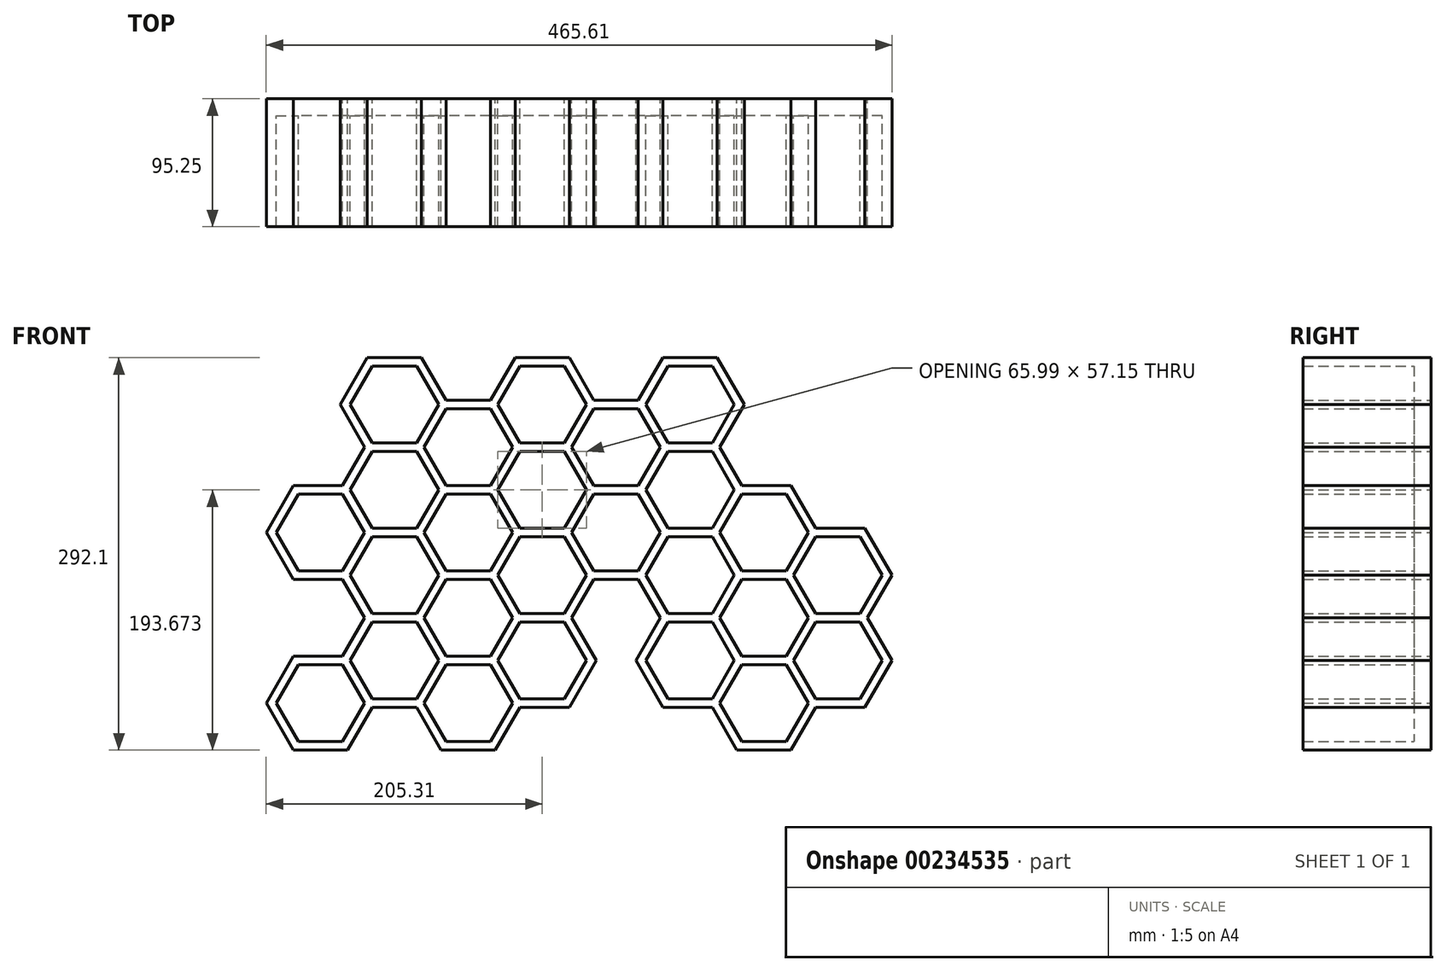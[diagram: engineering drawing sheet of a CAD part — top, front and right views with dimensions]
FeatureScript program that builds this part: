
annotation { "Feature Type Name" : "Feature", "Feature Type Description" : "" }
export const myFeature = defineFeature(function(context is Context, id is Id, definition is map)
    precondition{}
    {
        {
            var Q0;
            Q0=qCreatedBy(makeId("Front.planeOp"),FACE);
            var sketch = newSketch(context, id + "F0", { "sketchPlane" : qUnion([Q0])});
            skLineSegment(sketch, "E0.1", {"start": v(-4.28, 35.04) * mm, "end": v(27.5, 35.04) * mm});
            skCircle(sketch, "E1.cCircle", {"center": v(-40.94, 35.04) * mm, "radius": 28.58 * mm, "construction": true});
            skLineSegment(sketch, "E1.0", {"start": v(-73.94, 35.04) * mm, "end": v(-57.44, 63.62) * mm});
            skLineSegment(sketch, "E1.1", {"start": v(-57.44, 63.62) * mm, "end": v(-24.44, 63.62) * mm});
            skLineSegment(sketch, "E1.2", {"start": v(-24.44, 63.62) * mm, "end": v(-7.94, 35.04) * mm});
            skLineSegment(sketch, "E1.3", {"start": v(-7.94, 35.04) * mm, "end": v(-24.44, 6.47) * mm});
            skLineSegment(sketch, "E1.4", {"start": v(-24.44, 6.47) * mm, "end": v(-57.44, 6.47) * mm});
            skLineSegment(sketch, "E1.5", {"start": v(-57.44, 6.47) * mm, "end": v(-73.94, 35.04) * mm});
            skPoint(sketch, "E1.0.midPoint", {"position": v(-65.69, 49.33) * mm});
            skCircle(sketch, "E2.cCircle", {"center": v(-40.94, 35.04) * mm, "radius": 31.75 * mm, "construction": true});
            skLineSegment(sketch, "E2.0", {"start": v(-77.6, 35.04) * mm, "end": v(-59.27, 66.8) * mm});
            skLineSegment(sketch, "E2.1", {"start": v(-59.27, 66.8) * mm, "end": v(-22.6, 66.8) * mm});
            skLineSegment(sketch, "E2.2", {"start": v(-22.6, 66.8) * mm, "end": v(-4.28, 35.04) * mm});
            skLineSegment(sketch, "E2.3", {"start": v(-4.28, 35.04) * mm, "end": v(-22.6, 3.3) * mm});
            skLineSegment(sketch, "E2.4", {"start": v(-22.6, 3.3) * mm, "end": v(-59.27, 3.3) * mm});
            skLineSegment(sketch, "E2.5", {"start": v(-59.27, 3.3) * mm, "end": v(-77.6, 35.04) * mm});
            skPoint(sketch, "E2.0.midPoint", {"position": v(-68.44, 50.92) * mm});
            skCircle(sketch, "E3.cCircle", {"center": v(-95.93, 3.3) * mm, "radius": 28.58 * mm, "construction": true});
            skLineSegment(sketch, "E3.0", {"start": v(-128.93, 3.3) * mm, "end": v(-112.43, 31.87) * mm});
            skLineSegment(sketch, "E3.1", {"start": v(-112.43, 31.87) * mm, "end": v(-79.43, 31.87) * mm});
            skLineSegment(sketch, "E3.2", {"start": v(-79.43, 31.87) * mm, "end": v(-62.94, 3.3) * mm});
            skLineSegment(sketch, "E3.3", {"start": v(-62.94, 3.3) * mm, "end": v(-79.43, -25.28) * mm});
            skLineSegment(sketch, "E3.4", {"start": v(-79.43, -25.28) * mm, "end": v(-112.43, -25.28) * mm});
            skLineSegment(sketch, "E3.5", {"start": v(-112.43, -25.28) * mm, "end": v(-128.93, 3.3) * mm});
            skPoint(sketch, "E3.0.midPoint", {"position": v(-120.68, 17.58) * mm});
            skCircle(sketch, "E4.cCircle", {"center": v(-95.93, 3.3) * mm, "radius": 31.75 * mm, "construction": true});
            skLineSegment(sketch, "E4.0", {"start": v(-132.6, 3.3) * mm, "end": v(-114.26, 35.04) * mm});
            skLineSegment(sketch, "E4.1", {"start": v(-114.26, 35.04) * mm, "end": v(-77.6, 35.04) * mm});
            skLineSegment(sketch, "E4.2", {"start": v(-77.6, 35.04) * mm, "end": v(-59.27, 3.3) * mm});
            skLineSegment(sketch, "E4.3", {"start": v(-59.27, 3.3) * mm, "end": v(-77.6, -28.46) * mm});
            skLineSegment(sketch, "E4.4", {"start": v(-77.6, -28.46) * mm, "end": v(-114.26, -28.46) * mm});
            skLineSegment(sketch, "E4.5", {"start": v(-114.26, -28.46) * mm, "end": v(-132.6, 3.3) * mm});
            skPoint(sketch, "E4.0.midPoint", {"position": v(-123.43, 19.17) * mm});
            skCircle(sketch, "E5.cCircle", {"center": v(-150.93, 35.04) * mm, "radius": 28.58 * mm, "construction": true});
            skLineSegment(sketch, "E5.0", {"start": v(-183.92, 35.04) * mm, "end": v(-167.42, 63.62) * mm});
            skLineSegment(sketch, "E5.1", {"start": v(-167.42, 63.62) * mm, "end": v(-134.43, 63.62) * mm});
            skLineSegment(sketch, "E5.2", {"start": v(-134.43, 63.62) * mm, "end": v(-117.93, 35.04) * mm});
            skLineSegment(sketch, "E5.3", {"start": v(-117.93, 35.04) * mm, "end": v(-134.43, 6.47) * mm});
            skLineSegment(sketch, "E5.4", {"start": v(-134.43, 6.47) * mm, "end": v(-167.42, 6.47) * mm});
            skLineSegment(sketch, "E5.5", {"start": v(-167.42, 6.47) * mm, "end": v(-183.92, 35.04) * mm});
            skPoint(sketch, "E5.0.midPoint", {"position": v(-175.67, 49.33) * mm});
            skCircle(sketch, "E6.cCircle", {"center": v(-150.93, 35.04) * mm, "radius": 31.75 * mm, "construction": true});
            skLineSegment(sketch, "E6.0", {"start": v(-187.59, 35.04) * mm, "end": v(-169.26, 66.8) * mm});
            skLineSegment(sketch, "E6.1", {"start": v(-169.26, 66.8) * mm, "end": v(-132.6, 66.8) * mm});
            skLineSegment(sketch, "E6.2", {"start": v(-132.6, 66.8) * mm, "end": v(-114.26, 35.04) * mm});
            skLineSegment(sketch, "E6.3", {"start": v(-114.26, 35.04) * mm, "end": v(-132.6, 3.3) * mm});
            skLineSegment(sketch, "E6.4", {"start": v(-132.6, 3.3) * mm, "end": v(-169.26, 3.3) * mm});
            skLineSegment(sketch, "E6.5", {"start": v(-169.26, 3.3) * mm, "end": v(-187.59, 35.04) * mm});
            skPoint(sketch, "E6.0.midPoint", {"position": v(-178.42, 50.92) * mm});
            skLineSegment(sketch, "E7.1", {"start": v(-221.8, 35.04) * mm, "end": v(-187.59, 35.04) * mm});
            skLineSegment(sketch, "E7.2", {"start": v(-187.59, 35.04) * mm, "end": v(-172.31, 6.35) * mm});
            skCircle(sketch, "E8.cCircle", {"center": v(-95.93, 66.8) * mm, "radius": 28.58 * mm, "construction": true});
            skLineSegment(sketch, "E8.0", {"start": v(-128.93, 66.8) * mm, "end": v(-112.43, 95.37) * mm});
            skLineSegment(sketch, "E8.1", {"start": v(-112.43, 95.37) * mm, "end": v(-79.43, 95.37) * mm});
            skLineSegment(sketch, "E8.2", {"start": v(-79.43, 95.37) * mm, "end": v(-62.94, 66.8) * mm});
            skLineSegment(sketch, "E8.3", {"start": v(-62.94, 66.8) * mm, "end": v(-79.43, 38.22) * mm});
            skLineSegment(sketch, "E8.4", {"start": v(-79.43, 38.22) * mm, "end": v(-112.43, 38.22) * mm});
            skLineSegment(sketch, "E8.5", {"start": v(-112.43, 38.22) * mm, "end": v(-128.93, 66.8) * mm});
            skPoint(sketch, "E8.0.midPoint", {"position": v(-120.68, 81.08) * mm});
            skCircle(sketch, "E9.cCircle", {"center": v(-95.93, 66.8) * mm, "radius": 31.75 * mm, "construction": true});
            skLineSegment(sketch, "E9.0", {"start": v(-132.6, 66.8) * mm, "end": v(-114.26, 98.54) * mm});
            skLineSegment(sketch, "E9.1", {"start": v(-114.26, 98.54) * mm, "end": v(-77.6, 98.54) * mm});
            skLineSegment(sketch, "E9.2", {"start": v(-77.6, 98.54) * mm, "end": v(-59.27, 66.8) * mm});
            skLineSegment(sketch, "E9.3", {"start": v(-59.27, 66.8) * mm, "end": v(-77.6, 35.04) * mm});
            skLineSegment(sketch, "E9.4", {"start": v(-77.6, 35.04) * mm, "end": v(-114.26, 35.04) * mm});
            skLineSegment(sketch, "E9.5", {"start": v(-114.26, 35.04) * mm, "end": v(-132.6, 66.8) * mm});
            skPoint(sketch, "E9.0.midPoint", {"position": v(-123.43, 82.67) * mm});
            skCircle(sketch, "E10.cCircle", {"center": v(-205.92, 66.8) * mm, "radius": 28.57 * mm, "construction": true});
            skLineSegment(sketch, "E10.0", {"start": v(-238.91, 66.8) * mm, "end": v(-222.42, 95.37) * mm});
            skLineSegment(sketch, "E10.1", {"start": v(-222.42, 95.37) * mm, "end": v(-189.42, 95.37) * mm});
            skLineSegment(sketch, "E10.2", {"start": v(-189.42, 95.37) * mm, "end": v(-172.92, 66.8) * mm});
            skLineSegment(sketch, "E10.3", {"start": v(-172.92, 66.8) * mm, "end": v(-189.42, 38.22) * mm});
            skLineSegment(sketch, "E10.4", {"start": v(-189.42, 38.22) * mm, "end": v(-222.42, 38.22) * mm});
            skLineSegment(sketch, "E10.5", {"start": v(-222.42, 38.22) * mm, "end": v(-238.91, 66.8) * mm});
            skPoint(sketch, "E10.0.midPoint", {"position": v(-230.66, 81.08) * mm});
            skCircle(sketch, "E11.cCircle", {"center": v(-205.92, 66.8) * mm, "radius": 31.75 * mm, "construction": true});
            skLineSegment(sketch, "E11.0", {"start": v(-242.58, 66.8) * mm, "end": v(-224.25, 98.54) * mm});
            skLineSegment(sketch, "E11.1", {"start": v(-224.25, 98.54) * mm, "end": v(-187.59, 98.54) * mm});
            skLineSegment(sketch, "E11.2", {"start": v(-187.59, 98.54) * mm, "end": v(-169.26, 66.8) * mm});
            skLineSegment(sketch, "E11.3", {"start": v(-169.26, 66.8) * mm, "end": v(-187.59, 35.04) * mm});
            skLineSegment(sketch, "E11.4", {"start": v(-187.59, 35.04) * mm, "end": v(-224.25, 35.04) * mm});
            skLineSegment(sketch, "E11.5", {"start": v(-224.25, 35.04) * mm, "end": v(-242.58, 66.8) * mm});
            skPoint(sketch, "E11.0.midPoint", {"position": v(-233.41, 82.67) * mm});
            skCircle(sketch, "E12.cCircle", {"center": v(14.05, 66.8) * mm, "radius": 28.58 * mm, "construction": true});
            skLineSegment(sketch, "E12.0", {"start": v(-18.94, 66.8) * mm, "end": v(-2.45, 95.37) * mm});
            skLineSegment(sketch, "E12.1", {"start": v(-2.45, 95.37) * mm, "end": v(30.55, 95.37) * mm});
            skLineSegment(sketch, "E12.2", {"start": v(30.55, 95.37) * mm, "end": v(47.05, 66.8) * mm});
            skLineSegment(sketch, "E12.3", {"start": v(47.05, 66.8) * mm, "end": v(30.55, 38.22) * mm});
            skLineSegment(sketch, "E12.4", {"start": v(30.55, 38.22) * mm, "end": v(-2.45, 38.22) * mm});
            skLineSegment(sketch, "E12.5", {"start": v(-2.45, 38.22) * mm, "end": v(-18.94, 66.8) * mm});
            skPoint(sketch, "E12.0.midPoint", {"position": v(-10.7, 81.08) * mm});
            skCircle(sketch, "E13.cCircle", {"center": v(14.05, 66.8) * mm, "radius": 31.75 * mm, "construction": true});
            skLineSegment(sketch, "E13.0", {"start": v(-22.6, 66.8) * mm, "end": v(-4.28, 98.54) * mm});
            skLineSegment(sketch, "E13.1", {"start": v(-4.28, 98.54) * mm, "end": v(32.38, 98.54) * mm});
            skLineSegment(sketch, "E13.2", {"start": v(32.38, 98.54) * mm, "end": v(50.71, 66.8) * mm});
            skLineSegment(sketch, "E13.3", {"start": v(50.71, 66.8) * mm, "end": v(32.38, 35.04) * mm});
            skLineSegment(sketch, "E13.4", {"start": v(32.38, 35.04) * mm, "end": v(-4.28, 35.04) * mm});
            skLineSegment(sketch, "E13.5", {"start": v(-4.28, 35.04) * mm, "end": v(-22.6, 66.8) * mm});
            skPoint(sketch, "E13.0.midPoint", {"position": v(-13.44, 82.67) * mm});
            skCircle(sketch, "E14.cCircle", {"center": v(-150.93, 98.54) * mm, "radius": 28.58 * mm, "construction": true});
            skLineSegment(sketch, "E14.0", {"start": v(-183.92, 98.54) * mm, "end": v(-167.42, 127.12) * mm});
            skLineSegment(sketch, "E14.1", {"start": v(-167.42, 127.12) * mm, "end": v(-134.43, 127.12) * mm});
            skLineSegment(sketch, "E14.2", {"start": v(-134.43, 127.12) * mm, "end": v(-117.93, 98.54) * mm});
            skLineSegment(sketch, "E14.3", {"start": v(-117.93, 98.54) * mm, "end": v(-134.43, 69.97) * mm});
            skLineSegment(sketch, "E14.4", {"start": v(-134.43, 69.97) * mm, "end": v(-167.42, 69.97) * mm});
            skLineSegment(sketch, "E14.5", {"start": v(-167.42, 69.97) * mm, "end": v(-183.92, 98.54) * mm});
            skPoint(sketch, "E14.0.midPoint", {"position": v(-175.67, 112.83) * mm});
            skCircle(sketch, "E15.cCircle", {"center": v(-150.93, 98.54) * mm, "radius": 31.75 * mm, "construction": true});
            skLineSegment(sketch, "E15.0", {"start": v(-187.59, 98.54) * mm, "end": v(-169.26, 130.3) * mm});
            skLineSegment(sketch, "E15.1", {"start": v(-169.26, 130.3) * mm, "end": v(-132.6, 130.3) * mm});
            skLineSegment(sketch, "E15.2", {"start": v(-132.6, 130.3) * mm, "end": v(-114.26, 98.54) * mm});
            skLineSegment(sketch, "E15.3", {"start": v(-114.26, 98.54) * mm, "end": v(-132.6, 66.8) * mm});
            skLineSegment(sketch, "E15.4", {"start": v(-132.6, 66.8) * mm, "end": v(-169.26, 66.8) * mm});
            skLineSegment(sketch, "E15.5", {"start": v(-169.26, 66.8) * mm, "end": v(-187.59, 98.54) * mm});
            skPoint(sketch, "E15.0.midPoint", {"position": v(-178.42, 114.42) * mm});
            skLineSegment(sketch, "E16.0", {"start": v(-77.6, 98.54) * mm, "end": v(-59.27, 130.3) * mm});
            skLineSegment(sketch, "E16.1", {"start": v(-59.27, 130.3) * mm, "end": v(-27.5, 130.3) * mm});
            skLineSegment(sketch, "E16.4", {"start": v(-27.5, 66.8) * mm, "end": v(-59.27, 66.8) * mm});
            skLineSegment(sketch, "E16.5", {"start": v(-59.27, 66.8) * mm, "end": v(-77.6, 98.54) * mm});
            skCircle(sketch, "E17.cCircle", {"center": v(-95.93, 130.3) * mm, "radius": 28.58 * mm, "construction": true});
            skLineSegment(sketch, "E17.0", {"start": v(-128.93, 130.3) * mm, "end": v(-112.43, 158.87) * mm});
            skLineSegment(sketch, "E17.1", {"start": v(-112.43, 158.87) * mm, "end": v(-79.43, 158.87) * mm});
            skLineSegment(sketch, "E17.2", {"start": v(-79.43, 158.87) * mm, "end": v(-62.94, 130.3) * mm});
            skLineSegment(sketch, "E17.3", {"start": v(-62.94, 130.3) * mm, "end": v(-79.43, 101.72) * mm});
            skLineSegment(sketch, "E17.4", {"start": v(-79.43, 101.72) * mm, "end": v(-112.43, 101.72) * mm});
            skLineSegment(sketch, "E17.5", {"start": v(-112.43, 101.72) * mm, "end": v(-128.93, 130.3) * mm});
            skPoint(sketch, "E17.0.midPoint", {"position": v(-120.68, 144.58) * mm});
            skCircle(sketch, "E18.cCircle", {"center": v(-95.93, 130.3) * mm, "radius": 31.75 * mm, "construction": true});
            skLineSegment(sketch, "E18.0", {"start": v(-132.6, 130.3) * mm, "end": v(-114.26, 162.04) * mm});
            skLineSegment(sketch, "E18.1", {"start": v(-114.26, 162.04) * mm, "end": v(-77.6, 162.04) * mm});
            skLineSegment(sketch, "E18.2", {"start": v(-77.6, 162.04) * mm, "end": v(-59.27, 130.3) * mm});
            skLineSegment(sketch, "E18.3", {"start": v(-59.27, 130.3) * mm, "end": v(-77.6, 98.54) * mm});
            skLineSegment(sketch, "E18.4", {"start": v(-77.6, 98.54) * mm, "end": v(-114.26, 98.54) * mm});
            skLineSegment(sketch, "E18.5", {"start": v(-114.26, 98.54) * mm, "end": v(-132.6, 130.3) * mm});
            skPoint(sketch, "E18.0.midPoint", {"position": v(-123.43, 146.17) * mm});
            skCircle(sketch, "E19.cCircle", {"center": v(-40.94, -28.46) * mm, "radius": 28.58 * mm, "construction": true});
            skLineSegment(sketch, "E19.0", {"start": v(-73.94, -28.46) * mm, "end": v(-57.44, 0.12) * mm});
            skLineSegment(sketch, "E19.1", {"start": v(-57.44, 0.12) * mm, "end": v(-24.44, 0.12) * mm});
            skLineSegment(sketch, "E19.2", {"start": v(-24.44, 0.12) * mm, "end": v(-7.94, -28.46) * mm});
            skLineSegment(sketch, "E19.3", {"start": v(-7.94, -28.46) * mm, "end": v(-24.44, -57.03) * mm});
            skLineSegment(sketch, "E19.4", {"start": v(-24.44, -57.03) * mm, "end": v(-57.44, -57.03) * mm});
            skLineSegment(sketch, "E19.5", {"start": v(-57.44, -57.03) * mm, "end": v(-73.94, -28.46) * mm});
            skPoint(sketch, "E19.0.midPoint", {"position": v(-65.69, -14.17) * mm});
            skCircle(sketch, "E20.cCircle", {"center": v(-40.94, -28.46) * mm, "radius": 31.75 * mm, "construction": true});
            skLineSegment(sketch, "E20.0", {"start": v(-77.6, -28.46) * mm, "end": v(-59.27, 3.3) * mm});
            skLineSegment(sketch, "E20.1", {"start": v(-59.27, 3.3) * mm, "end": v(-22.6, 3.3) * mm});
            skLineSegment(sketch, "E20.2", {"start": v(-22.6, 3.3) * mm, "end": v(-4.28, -28.46) * mm});
            skLineSegment(sketch, "E20.3", {"start": v(-4.28, -28.46) * mm, "end": v(-22.6, -60.2) * mm});
            skLineSegment(sketch, "E20.4", {"start": v(-22.6, -60.2) * mm, "end": v(-59.27, -60.2) * mm});
            skLineSegment(sketch, "E20.5", {"start": v(-59.27, -60.2) * mm, "end": v(-77.6, -28.46) * mm});
            skPoint(sketch, "E20.0.midPoint", {"position": v(-68.44, -12.58) * mm});
            skCircle(sketch, "E21.cCircle", {"center": v(-150.93, -28.46) * mm, "radius": 28.58 * mm, "construction": true});
            skLineSegment(sketch, "E21.0", {"start": v(-183.92, -28.46) * mm, "end": v(-167.42, 0.12) * mm});
            skLineSegment(sketch, "E21.1", {"start": v(-167.42, 0.12) * mm, "end": v(-134.43, 0.12) * mm});
            skLineSegment(sketch, "E21.2", {"start": v(-134.43, 0.12) * mm, "end": v(-117.93, -28.46) * mm});
            skLineSegment(sketch, "E21.3", {"start": v(-117.93, -28.46) * mm, "end": v(-134.43, -57.03) * mm});
            skLineSegment(sketch, "E21.4", {"start": v(-134.43, -57.03) * mm, "end": v(-167.42, -57.03) * mm});
            skLineSegment(sketch, "E21.5", {"start": v(-167.42, -57.03) * mm, "end": v(-183.92, -28.46) * mm});
            skPoint(sketch, "E21.0.midPoint", {"position": v(-175.67, -14.17) * mm});
            skCircle(sketch, "E22.cCircle", {"center": v(-150.93, -28.46) * mm, "radius": 31.75 * mm, "construction": true});
            skLineSegment(sketch, "E22.0", {"start": v(-187.59, -28.46) * mm, "end": v(-169.26, 3.3) * mm});
            skLineSegment(sketch, "E22.1", {"start": v(-169.26, 3.3) * mm, "end": v(-132.6, 3.3) * mm});
            skLineSegment(sketch, "E22.2", {"start": v(-132.6, 3.3) * mm, "end": v(-114.26, -28.46) * mm});
            skLineSegment(sketch, "E22.3", {"start": v(-114.26, -28.46) * mm, "end": v(-132.6, -60.2) * mm});
            skLineSegment(sketch, "E22.4", {"start": v(-132.6, -60.2) * mm, "end": v(-169.26, -60.2) * mm});
            skLineSegment(sketch, "E22.5", {"start": v(-169.26, -60.2) * mm, "end": v(-187.59, -28.46) * mm});
            skPoint(sketch, "E22.0.midPoint", {"position": v(-178.42, -12.58) * mm});
            skCircle(sketch, "E23.cCircle", {"center": v(-95.93, -60.2) * mm, "radius": 28.57 * mm, "construction": true});
            skLineSegment(sketch, "E23.0", {"start": v(-128.93, -60.2) * mm, "end": v(-112.43, -31.63) * mm});
            skLineSegment(sketch, "E23.1", {"start": v(-112.43, -31.63) * mm, "end": v(-79.43, -31.63) * mm});
            skLineSegment(sketch, "E23.2", {"start": v(-79.43, -31.63) * mm, "end": v(-62.94, -60.2) * mm});
            skLineSegment(sketch, "E23.3", {"start": v(-62.94, -60.2) * mm, "end": v(-79.43, -88.78) * mm});
            skLineSegment(sketch, "E23.4", {"start": v(-79.43, -88.78) * mm, "end": v(-112.43, -88.78) * mm});
            skLineSegment(sketch, "E23.5", {"start": v(-112.43, -88.78) * mm, "end": v(-128.93, -60.2) * mm});
            skPoint(sketch, "E23.0.midPoint", {"position": v(-120.68, -45.92) * mm});
            skCircle(sketch, "E24.cCircle", {"center": v(-95.93, -60.2) * mm, "radius": 31.75 * mm, "construction": true});
            skLineSegment(sketch, "E24.0", {"start": v(-132.6, -60.2) * mm, "end": v(-114.26, -28.46) * mm});
            skLineSegment(sketch, "E24.1", {"start": v(-114.26, -28.46) * mm, "end": v(-77.6, -28.46) * mm});
            skLineSegment(sketch, "E24.2", {"start": v(-77.6, -28.46) * mm, "end": v(-59.27, -60.2) * mm});
            skLineSegment(sketch, "E24.3", {"start": v(-59.27, -60.2) * mm, "end": v(-77.6, -91.96) * mm});
            skLineSegment(sketch, "E24.4", {"start": v(-77.6, -91.96) * mm, "end": v(-114.26, -91.96) * mm});
            skLineSegment(sketch, "E24.5", {"start": v(-114.26, -91.96) * mm, "end": v(-132.6, -60.2) * mm});
            skPoint(sketch, "E24.0.midPoint", {"position": v(-123.43, -44.33) * mm});
            skLineSegment(sketch, "E25.4", {"start": v(-190.64, 98.54) * mm, "end": v(-224.25, 98.54) * mm});
            skCircle(sketch, "E26.cCircle", {"center": v(-150.93, 162.04) * mm, "radius": 28.58 * mm, "construction": true});
            skLineSegment(sketch, "E26.0", {"start": v(-183.92, 162.04) * mm, "end": v(-167.42, 190.62) * mm});
            skLineSegment(sketch, "E26.1", {"start": v(-167.42, 190.62) * mm, "end": v(-134.43, 190.62) * mm});
            skLineSegment(sketch, "E26.2", {"start": v(-134.43, 190.62) * mm, "end": v(-117.93, 162.04) * mm});
            skLineSegment(sketch, "E26.3", {"start": v(-117.93, 162.04) * mm, "end": v(-134.43, 133.47) * mm});
            skLineSegment(sketch, "E26.4", {"start": v(-134.43, 133.47) * mm, "end": v(-167.42, 133.47) * mm});
            skLineSegment(sketch, "E26.5", {"start": v(-167.42, 133.47) * mm, "end": v(-183.92, 162.04) * mm});
            skPoint(sketch, "E26.0.midPoint", {"position": v(-175.67, 176.33) * mm});
            skCircle(sketch, "E27.cCircle", {"center": v(-150.93, 162.04) * mm, "radius": 31.75 * mm, "construction": true});
            skLineSegment(sketch, "E27.0", {"start": v(-187.59, 162.04) * mm, "end": v(-169.26, 193.8) * mm});
            skLineSegment(sketch, "E27.1", {"start": v(-169.26, 193.8) * mm, "end": v(-132.6, 193.8) * mm});
            skLineSegment(sketch, "E27.2", {"start": v(-132.6, 193.8) * mm, "end": v(-114.26, 162.04) * mm});
            skLineSegment(sketch, "E27.3", {"start": v(-114.26, 162.04) * mm, "end": v(-132.6, 130.3) * mm});
            skLineSegment(sketch, "E27.4", {"start": v(-132.6, 130.3) * mm, "end": v(-169.26, 130.3) * mm});
            skLineSegment(sketch, "E27.5", {"start": v(-169.26, 130.3) * mm, "end": v(-187.59, 162.04) * mm});
            skPoint(sketch, "E27.0.midPoint", {"position": v(-178.42, 177.92) * mm});
            skCircle(sketch, "E28.cCircle", {"center": v(-40.94, 162.04) * mm, "radius": 28.58 * mm, "construction": true});
            skLineSegment(sketch, "E28.0", {"start": v(-73.94, 162.04) * mm, "end": v(-57.44, 190.62) * mm});
            skLineSegment(sketch, "E28.1", {"start": v(-57.44, 190.62) * mm, "end": v(-24.44, 190.62) * mm});
            skLineSegment(sketch, "E28.2", {"start": v(-24.44, 190.62) * mm, "end": v(-7.94, 162.04) * mm});
            skLineSegment(sketch, "E28.3", {"start": v(-7.94, 162.04) * mm, "end": v(-24.44, 133.47) * mm});
            skLineSegment(sketch, "E28.4", {"start": v(-24.44, 133.47) * mm, "end": v(-57.44, 133.47) * mm});
            skLineSegment(sketch, "E28.5", {"start": v(-57.44, 133.47) * mm, "end": v(-73.94, 162.04) * mm});
            skCircle(sketch, "E29.cCircle", {"center": v(-40.94, 162.04) * mm, "radius": 31.75 * mm, "construction": true});
            skLineSegment(sketch, "E29.0", {"start": v(-77.6, 162.04) * mm, "end": v(-59.27, 193.8) * mm});
            skLineSegment(sketch, "E29.1", {"start": v(-59.27, 193.8) * mm, "end": v(-22.6, 193.8) * mm});
            skLineSegment(sketch, "E29.2", {"start": v(-22.6, 193.8) * mm, "end": v(-4.28, 162.04) * mm});
            skLineSegment(sketch, "E29.3", {"start": v(-4.28, 162.04) * mm, "end": v(-22.6, 130.3) * mm});
            skLineSegment(sketch, "E29.4", {"start": v(-22.6, 130.3) * mm, "end": v(-59.27, 130.3) * mm});
            skLineSegment(sketch, "E29.5", {"start": v(-59.27, 130.3) * mm, "end": v(-77.6, 162.04) * mm});
            skPoint(sketch, "E29.0.midPoint", {"position": v(-68.44, 177.92) * mm});
            skCircle(sketch, "E30.cCircle", {"center": v(14.05, 130.3) * mm, "radius": 28.57 * mm, "construction": true});
            skLineSegment(sketch, "E30.0", {"start": v(-18.94, 130.3) * mm, "end": v(-2.45, 158.87) * mm});
            skLineSegment(sketch, "E30.1", {"start": v(-2.45, 158.87) * mm, "end": v(30.55, 158.87) * mm});
            skLineSegment(sketch, "E30.2", {"start": v(30.55, 158.87) * mm, "end": v(47.05, 130.3) * mm});
            skLineSegment(sketch, "E30.3", {"start": v(47.05, 130.3) * mm, "end": v(30.55, 101.72) * mm});
            skLineSegment(sketch, "E30.4", {"start": v(30.55, 101.72) * mm, "end": v(-2.45, 101.72) * mm});
            skLineSegment(sketch, "E30.5", {"start": v(-2.45, 101.72) * mm, "end": v(-18.94, 130.3) * mm});
            skPoint(sketch, "E30.0.midPoint", {"position": v(-10.7, 144.58) * mm});
            skCircle(sketch, "E31.cCircle", {"center": v(14.05, 130.3) * mm, "radius": 31.75 * mm, "construction": true});
            skLineSegment(sketch, "E31.0", {"start": v(-22.6, 130.3) * mm, "end": v(-4.28, 162.04) * mm});
            skLineSegment(sketch, "E31.1", {"start": v(-4.28, 162.04) * mm, "end": v(32.38, 162.04) * mm});
            skLineSegment(sketch, "E31.2", {"start": v(32.38, 162.04) * mm, "end": v(50.71, 130.3) * mm});
            skLineSegment(sketch, "E31.3", {"start": v(50.71, 130.3) * mm, "end": v(32.38, 98.54) * mm});
            skLineSegment(sketch, "E31.4", {"start": v(32.38, 98.54) * mm, "end": v(-4.28, 98.54) * mm});
            skLineSegment(sketch, "E31.5", {"start": v(-4.28, 98.54) * mm, "end": v(-22.6, 130.3) * mm});
            skPoint(sketch, "E31.0.midPoint", {"position": v(-13.44, 146.17) * mm});
            skCircle(sketch, "E32.cCircle", {"center": v(-205.92, -60.2) * mm, "radius": 28.58 * mm, "construction": true});
            skLineSegment(sketch, "E32.0", {"start": v(-238.91, -60.2) * mm, "end": v(-222.42, -31.63) * mm});
            skLineSegment(sketch, "E32.1", {"start": v(-222.42, -31.63) * mm, "end": v(-189.42, -31.63) * mm});
            skLineSegment(sketch, "E32.2", {"start": v(-189.42, -31.63) * mm, "end": v(-172.92, -60.2) * mm});
            skLineSegment(sketch, "E32.3", {"start": v(-172.92, -60.2) * mm, "end": v(-189.42, -88.78) * mm});
            skLineSegment(sketch, "E32.4", {"start": v(-189.42, -88.78) * mm, "end": v(-222.42, -88.78) * mm});
            skLineSegment(sketch, "E32.5", {"start": v(-222.42, -88.78) * mm, "end": v(-238.91, -60.2) * mm});
            skPoint(sketch, "E32.0.midPoint", {"position": v(-230.66, -45.92) * mm});
            skCircle(sketch, "E33.cCircle", {"center": v(-205.92, -60.2) * mm, "radius": 31.75 * mm, "construction": true});
            skLineSegment(sketch, "E33.0", {"start": v(-242.58, -60.2) * mm, "end": v(-224.25, -28.46) * mm});
            skLineSegment(sketch, "E33.1", {"start": v(-224.25, -28.46) * mm, "end": v(-187.59, -28.46) * mm});
            skLineSegment(sketch, "E33.2", {"start": v(-187.59, -28.46) * mm, "end": v(-169.26, -60.2) * mm});
            skLineSegment(sketch, "E33.3", {"start": v(-169.26, -60.2) * mm, "end": v(-187.59, -91.96) * mm});
            skLineSegment(sketch, "E33.4", {"start": v(-187.59, -91.96) * mm, "end": v(-224.25, -91.96) * mm});
            skLineSegment(sketch, "E33.5", {"start": v(-224.25, -91.96) * mm, "end": v(-242.58, -60.2) * mm});
            skPoint(sketch, "E33.0.midPoint", {"position": v(-233.41, -44.33) * mm});
            skCircle(sketch, "E34.cCircle", {"center": v(69.05, 162.04) * mm, "radius": 28.58 * mm, "construction": true});
            skLineSegment(sketch, "E34.0", {"start": v(36.05, 162.04) * mm, "end": v(52.55, 190.62) * mm});
            skLineSegment(sketch, "E34.1", {"start": v(52.55, 190.62) * mm, "end": v(85.54, 190.62) * mm});
            skLineSegment(sketch, "E34.2", {"start": v(85.54, 190.62) * mm, "end": v(102.04, 162.04) * mm});
            skLineSegment(sketch, "E34.3", {"start": v(102.04, 162.04) * mm, "end": v(85.54, 133.47) * mm});
            skLineSegment(sketch, "E34.4", {"start": v(85.54, 133.47) * mm, "end": v(52.55, 133.47) * mm});
            skLineSegment(sketch, "E34.5", {"start": v(52.55, 133.47) * mm, "end": v(36.05, 162.04) * mm});
            skPoint(sketch, "E34.0.midPoint", {"position": v(44.3, 176.33) * mm});
            skCircle(sketch, "E35.cCircle", {"center": v(69.05, 162.04) * mm, "radius": 31.75 * mm, "construction": true});
            skLineSegment(sketch, "E35.0", {"start": v(32.38, 162.04) * mm, "end": v(50.71, 193.8) * mm});
            skLineSegment(sketch, "E35.1", {"start": v(50.71, 193.8) * mm, "end": v(87.38, 193.8) * mm});
            skLineSegment(sketch, "E35.2", {"start": v(87.38, 193.8) * mm, "end": v(105.7, 162.04) * mm});
            skLineSegment(sketch, "E35.3", {"start": v(105.7, 162.04) * mm, "end": v(87.38, 130.3) * mm});
            skLineSegment(sketch, "E35.4", {"start": v(87.38, 130.3) * mm, "end": v(50.71, 130.3) * mm});
            skLineSegment(sketch, "E35.5", {"start": v(50.71, 130.3) * mm, "end": v(32.38, 162.04) * mm});
            skPoint(sketch, "E35.0.midPoint", {"position": v(41.55, 177.92) * mm});
            skCircle(sketch, "E36.cCircle", {"center": v(69.05, 98.54) * mm, "radius": 28.58 * mm, "construction": true});
            skLineSegment(sketch, "E36.0", {"start": v(36.05, 98.54) * mm, "end": v(52.55, 127.12) * mm});
            skLineSegment(sketch, "E36.1", {"start": v(52.55, 127.12) * mm, "end": v(85.54, 127.12) * mm});
            skLineSegment(sketch, "E36.2", {"start": v(85.54, 127.12) * mm, "end": v(102.04, 98.54) * mm});
            skLineSegment(sketch, "E36.3", {"start": v(102.04, 98.54) * mm, "end": v(85.54, 69.97) * mm});
            skLineSegment(sketch, "E36.4", {"start": v(85.54, 69.97) * mm, "end": v(52.55, 69.97) * mm});
            skLineSegment(sketch, "E36.5", {"start": v(52.55, 69.97) * mm, "end": v(36.05, 98.54) * mm});
            skPoint(sketch, "E36.0.midPoint", {"position": v(44.3, 112.83) * mm});
            skCircle(sketch, "E37.cCircle", {"center": v(69.05, 98.54) * mm, "radius": 31.75 * mm, "construction": true});
            skLineSegment(sketch, "E37.0", {"start": v(32.38, 98.54) * mm, "end": v(50.71, 130.3) * mm});
            skLineSegment(sketch, "E37.1", {"start": v(50.71, 130.3) * mm, "end": v(87.38, 130.3) * mm});
            skLineSegment(sketch, "E37.2", {"start": v(87.38, 130.3) * mm, "end": v(105.7, 98.54) * mm});
            skLineSegment(sketch, "E37.3", {"start": v(105.7, 98.54) * mm, "end": v(87.38, 66.8) * mm});
            skLineSegment(sketch, "E37.4", {"start": v(87.38, 66.8) * mm, "end": v(50.71, 66.8) * mm});
            skLineSegment(sketch, "E37.5", {"start": v(50.71, 66.8) * mm, "end": v(32.38, 98.54) * mm});
            skPoint(sketch, "E37.0.midPoint", {"position": v(41.55, 114.42) * mm});
            skCircle(sketch, "E38.cCircle", {"center": v(69.05, 35.04) * mm, "radius": 28.58 * mm, "construction": true});
            skLineSegment(sketch, "E38.0", {"start": v(36.05, 35.04) * mm, "end": v(52.55, 63.62) * mm});
            skLineSegment(sketch, "E38.1", {"start": v(52.55, 63.62) * mm, "end": v(85.54, 63.62) * mm});
            skLineSegment(sketch, "E38.2", {"start": v(85.54, 63.62) * mm, "end": v(102.04, 35.04) * mm});
            skLineSegment(sketch, "E38.3", {"start": v(102.04, 35.04) * mm, "end": v(85.54, 6.47) * mm});
            skLineSegment(sketch, "E38.4", {"start": v(85.54, 6.47) * mm, "end": v(52.55, 6.47) * mm});
            skLineSegment(sketch, "E38.5", {"start": v(52.55, 6.47) * mm, "end": v(36.05, 35.04) * mm});
            skPoint(sketch, "E38.0.midPoint", {"position": v(44.3, 49.33) * mm});
            skCircle(sketch, "E39.cCircle", {"center": v(69.05, 35.04) * mm, "radius": 31.75 * mm, "construction": true});
            skLineSegment(sketch, "E39.0", {"start": v(32.38, 35.04) * mm, "end": v(50.71, 66.8) * mm});
            skLineSegment(sketch, "E39.1", {"start": v(50.71, 66.8) * mm, "end": v(87.38, 66.8) * mm});
            skLineSegment(sketch, "E39.2", {"start": v(87.38, 66.8) * mm, "end": v(105.7, 35.04) * mm});
            skLineSegment(sketch, "E39.3", {"start": v(105.7, 35.04) * mm, "end": v(87.38, 3.3) * mm});
            skLineSegment(sketch, "E39.4", {"start": v(87.38, 3.3) * mm, "end": v(50.71, 3.3) * mm});
            skLineSegment(sketch, "E39.5", {"start": v(50.71, 3.3) * mm, "end": v(32.38, 35.04) * mm});
            skPoint(sketch, "E39.0.midPoint", {"position": v(41.55, 50.92) * mm});
            skCircle(sketch, "E40.cCircle", {"center": v(69.05, -28.46) * mm, "radius": 28.57 * mm, "construction": true});
            skLineSegment(sketch, "E40.0", {"start": v(36.05, -28.46) * mm, "end": v(52.55, 0.12) * mm});
            skLineSegment(sketch, "E40.1", {"start": v(52.55, 0.12) * mm, "end": v(85.54, 0.12) * mm});
            skLineSegment(sketch, "E40.2", {"start": v(85.54, 0.12) * mm, "end": v(102.04, -28.46) * mm});
            skLineSegment(sketch, "E40.3", {"start": v(102.04, -28.46) * mm, "end": v(85.54, -57.03) * mm});
            skLineSegment(sketch, "E40.4", {"start": v(85.54, -57.03) * mm, "end": v(52.55, -57.03) * mm});
            skLineSegment(sketch, "E40.5", {"start": v(52.55, -57.03) * mm, "end": v(36.05, -28.46) * mm});
            skPoint(sketch, "E40.0.midPoint", {"position": v(44.3, -14.17) * mm});
            skCircle(sketch, "E41.cCircle", {"center": v(69.05, -28.46) * mm, "radius": 31.75 * mm, "construction": true});
            skLineSegment(sketch, "E41.0", {"start": v(32.38, -28.46) * mm, "end": v(50.71, 3.3) * mm});
            skLineSegment(sketch, "E41.1", {"start": v(50.71, 3.3) * mm, "end": v(87.38, 3.3) * mm});
            skLineSegment(sketch, "E41.2", {"start": v(87.38, 3.3) * mm, "end": v(105.7, -28.46) * mm});
            skLineSegment(sketch, "E41.3", {"start": v(105.7, -28.46) * mm, "end": v(87.38, -60.2) * mm});
            skLineSegment(sketch, "E41.4", {"start": v(87.38, -60.2) * mm, "end": v(50.71, -60.2) * mm});
            skLineSegment(sketch, "E41.5", {"start": v(50.71, -60.2) * mm, "end": v(32.38, -28.46) * mm});
            skPoint(sketch, "E41.0.midPoint", {"position": v(41.55, -12.58) * mm});
            skCircle(sketch, "E42.cCircle", {"center": v(124.04, 3.3) * mm, "radius": 28.58 * mm, "construction": true});
            skLineSegment(sketch, "E42.0", {"start": v(91.04, 3.3) * mm, "end": v(107.54, 31.87) * mm});
            skLineSegment(sketch, "E42.1", {"start": v(107.54, 31.87) * mm, "end": v(140.54, 31.87) * mm});
            skLineSegment(sketch, "E42.2", {"start": v(140.54, 31.87) * mm, "end": v(157.03, 3.3) * mm});
            skLineSegment(sketch, "E42.3", {"start": v(157.03, 3.3) * mm, "end": v(140.54, -25.28) * mm});
            skLineSegment(sketch, "E42.4", {"start": v(140.54, -25.28) * mm, "end": v(107.54, -25.28) * mm});
            skLineSegment(sketch, "E42.5", {"start": v(107.54, -25.28) * mm, "end": v(91.04, 3.3) * mm});
            skPoint(sketch, "E42.0.midPoint", {"position": v(99.3, 17.58) * mm});
            skCircle(sketch, "E43.cCircle", {"center": v(124.04, 3.3) * mm, "radius": 31.75 * mm, "construction": true});
            skLineSegment(sketch, "E43.0", {"start": v(87.38, 3.3) * mm, "end": v(105.7, 35.04) * mm});
            skLineSegment(sketch, "E43.1", {"start": v(105.7, 35.04) * mm, "end": v(142.37, 35.04) * mm});
            skLineSegment(sketch, "E43.2", {"start": v(142.37, 35.04) * mm, "end": v(160.7, 3.3) * mm});
            skLineSegment(sketch, "E43.3", {"start": v(160.7, 3.3) * mm, "end": v(142.37, -28.46) * mm});
            skLineSegment(sketch, "E43.4", {"start": v(142.37, -28.46) * mm, "end": v(105.7, -28.46) * mm});
            skLineSegment(sketch, "E43.5", {"start": v(105.7, -28.46) * mm, "end": v(87.38, 3.3) * mm});
            skPoint(sketch, "E43.0.midPoint", {"position": v(96.54, 19.17) * mm});
            skCircle(sketch, "E44.cCircle", {"center": v(124.04, 66.8) * mm, "radius": 28.58 * mm, "construction": true});
            skLineSegment(sketch, "E44.0", {"start": v(91.04, 66.8) * mm, "end": v(107.54, 95.37) * mm});
            skLineSegment(sketch, "E44.1", {"start": v(107.54, 95.37) * mm, "end": v(140.54, 95.37) * mm});
            skLineSegment(sketch, "E44.2", {"start": v(140.54, 95.37) * mm, "end": v(157.03, 66.8) * mm});
            skLineSegment(sketch, "E44.3", {"start": v(157.03, 66.8) * mm, "end": v(140.54, 38.22) * mm});
            skLineSegment(sketch, "E44.4", {"start": v(140.54, 38.22) * mm, "end": v(107.54, 38.22) * mm});
            skLineSegment(sketch, "E44.5", {"start": v(107.54, 38.22) * mm, "end": v(91.04, 66.8) * mm});
            skPoint(sketch, "E44.0.midPoint", {"position": v(99.3, 81.08) * mm});
            skCircle(sketch, "E45.cCircle", {"center": v(124.04, 66.8) * mm, "radius": 31.75 * mm, "construction": true});
            skLineSegment(sketch, "E45.0", {"start": v(87.38, 66.8) * mm, "end": v(105.7, 98.54) * mm});
            skLineSegment(sketch, "E45.1", {"start": v(105.7, 98.54) * mm, "end": v(142.37, 98.54) * mm});
            skLineSegment(sketch, "E45.2", {"start": v(142.37, 98.54) * mm, "end": v(160.7, 66.8) * mm});
            skLineSegment(sketch, "E45.3", {"start": v(160.7, 66.8) * mm, "end": v(142.37, 35.04) * mm});
            skLineSegment(sketch, "E45.4", {"start": v(142.37, 35.04) * mm, "end": v(105.7, 35.04) * mm});
            skLineSegment(sketch, "E45.5", {"start": v(105.7, 35.04) * mm, "end": v(87.38, 66.8) * mm});
            skPoint(sketch, "E45.0.midPoint", {"position": v(96.54, 82.67) * mm});
            skCircle(sketch, "E46.cCircle", {"center": v(124.04, -60.2) * mm, "radius": 28.58 * mm, "construction": true});
            skLineSegment(sketch, "E46.0", {"start": v(91.04, -60.2) * mm, "end": v(107.54, -31.63) * mm});
            skLineSegment(sketch, "E46.1", {"start": v(107.54, -31.63) * mm, "end": v(140.54, -31.63) * mm});
            skLineSegment(sketch, "E46.2", {"start": v(140.54, -31.63) * mm, "end": v(157.03, -60.2) * mm});
            skLineSegment(sketch, "E46.3", {"start": v(157.03, -60.2) * mm, "end": v(140.54, -88.78) * mm});
            skLineSegment(sketch, "E46.4", {"start": v(140.54, -88.78) * mm, "end": v(107.54, -88.78) * mm});
            skLineSegment(sketch, "E46.5", {"start": v(107.54, -88.78) * mm, "end": v(91.04, -60.2) * mm});
            skPoint(sketch, "E46.0.midPoint", {"position": v(99.3, -45.92) * mm});
            skCircle(sketch, "E47.cCircle", {"center": v(124.04, -60.2) * mm, "radius": 31.75 * mm, "construction": true});
            skLineSegment(sketch, "E47.0", {"start": v(87.38, -60.2) * mm, "end": v(105.7, -28.46) * mm});
            skLineSegment(sketch, "E47.1", {"start": v(105.7, -28.46) * mm, "end": v(142.37, -28.46) * mm});
            skLineSegment(sketch, "E47.2", {"start": v(142.37, -28.46) * mm, "end": v(160.7, -60.2) * mm});
            skLineSegment(sketch, "E47.3", {"start": v(160.7, -60.2) * mm, "end": v(142.37, -91.96) * mm});
            skLineSegment(sketch, "E47.4", {"start": v(142.37, -91.96) * mm, "end": v(105.7, -91.96) * mm});
            skLineSegment(sketch, "E47.5", {"start": v(105.7, -91.96) * mm, "end": v(87.38, -60.2) * mm});
            skPoint(sketch, "E47.0.midPoint", {"position": v(96.54, -44.33) * mm});
            skCircle(sketch, "E48.cCircle", {"center": v(179.03, -28.46) * mm, "radius": 28.57 * mm, "construction": true});
            skLineSegment(sketch, "E48.0", {"start": v(146.03, -28.46) * mm, "end": v(162.53, 0.12) * mm});
            skLineSegment(sketch, "E48.1", {"start": v(162.53, 0.12) * mm, "end": v(195.53, 0.12) * mm});
            skLineSegment(sketch, "E48.2", {"start": v(195.53, 0.12) * mm, "end": v(212.03, -28.46) * mm});
            skLineSegment(sketch, "E48.3", {"start": v(212.03, -28.46) * mm, "end": v(195.53, -57.03) * mm});
            skLineSegment(sketch, "E48.4", {"start": v(195.53, -57.03) * mm, "end": v(162.53, -57.03) * mm});
            skLineSegment(sketch, "E48.5", {"start": v(162.53, -57.03) * mm, "end": v(146.03, -28.46) * mm});
            skPoint(sketch, "E48.0.midPoint", {"position": v(154.28, -14.17) * mm});
            skCircle(sketch, "E49.cCircle", {"center": v(179.03, -28.46) * mm, "radius": 31.75 * mm, "construction": true});
            skLineSegment(sketch, "E49.0", {"start": v(142.37, -28.46) * mm, "end": v(160.7, 3.3) * mm});
            skLineSegment(sketch, "E49.1", {"start": v(160.7, 3.3) * mm, "end": v(197.36, 3.3) * mm});
            skLineSegment(sketch, "E49.2", {"start": v(197.36, 3.3) * mm, "end": v(215.7, -28.46) * mm});
            skLineSegment(sketch, "E49.3", {"start": v(215.7, -28.46) * mm, "end": v(197.36, -60.2) * mm});
            skLineSegment(sketch, "E49.4", {"start": v(197.36, -60.2) * mm, "end": v(160.7, -60.2) * mm});
            skLineSegment(sketch, "E49.5", {"start": v(160.7, -60.2) * mm, "end": v(142.37, -28.46) * mm});
            skPoint(sketch, "E49.0.midPoint", {"position": v(151.53, -12.58) * mm});
            skCircle(sketch, "E50.cCircle", {"center": v(179.03, 35.04) * mm, "radius": 28.58 * mm, "construction": true});
            skLineSegment(sketch, "E50.0", {"start": v(146.03, 35.04) * mm, "end": v(162.53, 63.62) * mm});
            skLineSegment(sketch, "E50.1", {"start": v(162.53, 63.62) * mm, "end": v(195.53, 63.62) * mm});
            skLineSegment(sketch, "E50.2", {"start": v(195.53, 63.62) * mm, "end": v(212.03, 35.04) * mm});
            skLineSegment(sketch, "E50.3", {"start": v(212.03, 35.04) * mm, "end": v(195.53, 6.47) * mm});
            skLineSegment(sketch, "E50.4", {"start": v(195.53, 6.47) * mm, "end": v(162.53, 6.47) * mm});
            skLineSegment(sketch, "E50.5", {"start": v(162.53, 6.47) * mm, "end": v(146.03, 35.04) * mm});
            skPoint(sketch, "E50.0.midPoint", {"position": v(154.28, 49.33) * mm});
            skCircle(sketch, "E51.cCircle", {"center": v(179.03, 35.04) * mm, "radius": 31.75 * mm, "construction": true});
            skLineSegment(sketch, "E51.0", {"start": v(142.37, 35.04) * mm, "end": v(160.7, 66.8) * mm});
            skLineSegment(sketch, "E51.1", {"start": v(160.7, 66.8) * mm, "end": v(197.36, 66.8) * mm});
            skLineSegment(sketch, "E51.2", {"start": v(197.36, 66.8) * mm, "end": v(215.7, 35.04) * mm});
            skLineSegment(sketch, "E51.3", {"start": v(215.7, 35.04) * mm, "end": v(197.36, 3.3) * mm});
            skLineSegment(sketch, "E51.4", {"start": v(197.36, 3.3) * mm, "end": v(160.7, 3.3) * mm});
            skLineSegment(sketch, "E51.5", {"start": v(160.7, 3.3) * mm, "end": v(142.37, 35.04) * mm});
            skPoint(sketch, "E51.0.midPoint", {"position": v(151.53, 50.92) * mm});
            skLineSegment(sketch, "E52", {"start": v(48.88, 196.97) * mm, "end": v(89.2, 196.97) * mm});
            skLineSegment(sketch, "E53", {"start": v(48.88, 196.97) * mm, "end": v(30.55, 165.22) * mm});
            skLineSegment(sketch, "E54", {"start": v(30.55, 165.22) * mm, "end": v(-2.45, 165.22) * mm});
            skLineSegment(sketch, "E55", {"start": v(-2.45, 165.22) * mm, "end": v(-20.78, 196.97) * mm});
            skLineSegment(sketch, "E56", {"start": v(-20.78, 196.97) * mm, "end": v(-61.1, 196.97) * mm});
            skLineSegment(sketch, "E57", {"start": v(-61.1, 196.97) * mm, "end": v(-79.43, 165.22) * mm});
            skLineSegment(sketch, "E58", {"start": v(-171.09, 196.97) * mm, "end": v(-191.25, 162.04) * mm});
            skLineSegment(sketch, "E59", {"start": v(-191.25, 162.04) * mm, "end": v(-172.92, 130.3) * mm});
            skLineSegment(sketch, "E60", {"start": v(-172.92, 130.3) * mm, "end": v(-189.42, 101.72) * mm});
            skLineSegment(sketch, "E61", {"start": v(-189.42, 101.72) * mm, "end": v(-226.08, 101.72) * mm});
            skLineSegment(sketch, "E62", {"start": v(-226.08, 101.72) * mm, "end": v(-246.25, 66.8) * mm});
            skLineSegment(sketch, "E63", {"start": v(-246.25, 66.8) * mm, "end": v(-226.08, 31.87) * mm});
            skLineSegment(sketch, "E64", {"start": v(-226.08, 31.87) * mm, "end": v(-189.42, 31.87) * mm});
            skLineSegment(sketch, "E65", {"start": v(-189.42, 31.87) * mm, "end": v(-172.92, 3.3) * mm});
            skLineSegment(sketch, "E66", {"start": v(-172.92, 3.3) * mm, "end": v(-189.42, -25.28) * mm});
            skLineSegment(sketch, "E67", {"start": v(-189.42, -25.28) * mm, "end": v(-226.08, -25.28) * mm});
            skLineSegment(sketch, "E68", {"start": v(-226.08, -25.28) * mm, "end": v(-246.25, -60.2) * mm});
            skLineSegment(sketch, "E69", {"start": v(-246.25, -60.2) * mm, "end": v(-226.08, -95.13) * mm});
            skLineSegment(sketch, "E70", {"start": v(-226.08, -95.13) * mm, "end": v(-185.75, -95.13) * mm});
            skLineSegment(sketch, "E71", {"start": v(-185.75, -95.13) * mm, "end": v(-167.42, -63.38) * mm});
            skLineSegment(sketch, "E72", {"start": v(-167.42, -63.38) * mm, "end": v(-134.43, -63.38) * mm});
            skLineSegment(sketch, "E73", {"start": v(-134.43, -63.38) * mm, "end": v(-116.1, -95.13) * mm});
            skLineSegment(sketch, "E74", {"start": v(-116.1, -95.13) * mm, "end": v(-75.77, -95.13) * mm});
            skLineSegment(sketch, "E75", {"start": v(-75.77, -95.13) * mm, "end": v(-57.44, -63.38) * mm});
            skLineSegment(sketch, "E76", {"start": v(-57.44, -63.38) * mm, "end": v(-20.78, -63.38) * mm});
            skLineSegment(sketch, "E77", {"start": v(-20.78, -63.38) * mm, "end": v(-0.61, -28.46) * mm});
            skLineSegment(sketch, "E78", {"start": v(30.55, 31.87) * mm, "end": v(47.05, 3.3) * mm});
            skLineSegment(sketch, "E79", {"start": v(47.05, 3.3) * mm, "end": v(28.72, -28.46) * mm});
            skLineSegment(sketch, "E80", {"start": v(-0.61, -28.46) * mm, "end": v(-18.94, 3.3) * mm});
            skLineSegment(sketch, "E81", {"start": v(-18.94, 3.3) * mm, "end": v(-2.45, 31.87) * mm});
            skLineSegment(sketch, "E82", {"start": v(-2.45, 31.87) * mm, "end": v(30.55, 31.87) * mm});
            skLineSegment(sketch, "E83", {"start": v(-171.09, 196.97) * mm, "end": v(-130.76, 196.97) * mm});
            skLineSegment(sketch, "E84", {"start": v(-130.76, 196.97) * mm, "end": v(-112.43, 165.22) * mm});
            skLineSegment(sketch, "E85", {"start": v(-112.43, 165.22) * mm, "end": v(-79.43, 165.22) * mm});
            skLineSegment(sketch, "E86", {"start": v(28.72, -28.46) * mm, "end": v(48.88, -63.38) * mm});
            skLineSegment(sketch, "E87", {"start": v(48.88, -63.38) * mm, "end": v(85.54, -63.38) * mm});
            skLineSegment(sketch, "E88", {"start": v(85.54, -63.38) * mm, "end": v(103.87, -95.13) * mm});
            skLineSegment(sketch, "E89", {"start": v(103.87, -95.13) * mm, "end": v(144.2, -95.13) * mm});
            skLineSegment(sketch, "E90", {"start": v(144.2, -95.13) * mm, "end": v(162.53, -63.38) * mm});
            skLineSegment(sketch, "E91", {"start": v(162.53, -63.38) * mm, "end": v(199.2, -63.38) * mm});
            skLineSegment(sketch, "E92", {"start": v(199.2, -63.38) * mm, "end": v(219.36, -28.46) * mm});
            skLineSegment(sketch, "E93", {"start": v(219.36, -28.46) * mm, "end": v(201.03, 3.3) * mm});
            skLineSegment(sketch, "E94", {"start": v(201.03, 3.3) * mm, "end": v(219.36, 35.04) * mm});
            skLineSegment(sketch, "E95", {"start": v(219.36, 35.04) * mm, "end": v(199.2, 69.97) * mm});
            skLineSegment(sketch, "E96", {"start": v(199.2, 69.97) * mm, "end": v(162.53, 69.97) * mm});
            skLineSegment(sketch, "E97", {"start": v(162.53, 69.97) * mm, "end": v(144.2, 101.72) * mm});
            skLineSegment(sketch, "E98", {"start": v(144.2, 101.72) * mm, "end": v(107.54, 101.72) * mm});
            skLineSegment(sketch, "E99", {"start": v(107.54, 101.72) * mm, "end": v(91.04, 130.3) * mm});
            skLineSegment(sketch, "E100", {"start": v(91.04, 130.3) * mm, "end": v(109.37, 162.04) * mm});
            skLineSegment(sketch, "E101", {"start": v(89.2, 196.97) * mm, "end": v(109.37, 162.04) * mm});
            skLineSegment(sketch, "E102", {"start": v(-57.44, 127.12) * mm, "end": v(-73.94, 98.54) * mm});
            skLineSegment(sketch, "E103", {"start": v(-73.94, 98.54) * mm, "end": v(-57.44, 69.97) * mm});
            skLineSegment(sketch, "E104", {"start": v(-57.44, 69.97) * mm, "end": v(-24.44, 69.97) * mm});
            skLineSegment(sketch, "E105", {"start": v(-24.44, 69.97) * mm, "end": v(-7.94, 98.54) * mm});
            skLineSegment(sketch, "E106", {"start": v(-7.94, 98.54) * mm, "end": v(-24.44, 127.12) * mm});
            skLineSegment(sketch, "E107", {"start": v(-24.44, 127.12) * mm, "end": v(-57.44, 127.12) * mm});
            skSolve(sketch);
        }
        {
            var Q0;
            Q0=makeQuery(id+"F0.imprint","IMPRINT",FACE,{"disambiguationData":[TD([[makeQuery(id+"F0.imprint","IMPRINT",EDGE,{"derivedFrom":sQuery(id+"F0.wireOp",EDGE,"E28.0")}),-1.0]])]});
            var Q1;
            Q1=makeQuery(id+"F0.imprint","IMPRINT",FACE,{"disambiguationData":[TD([[makeQuery(id+"F0.imprint","IMPRINT",EDGE,{"derivedFrom":sQuery(id+"F0.wireOp",EDGE,"E48.0")}),-1.0]])]});
            var Q2;
            Q2=makeQuery(id+"F0.imprint","IMPRINT",FACE,{"disambiguationData":[TD([[makeQuery(id+"F0.imprint","IMPRINT",EDGE,{"derivedFrom":sQuery(id+"F0.wireOp",EDGE,"E34.0")}),-1.0]])]});
            var Q3;
            Q3=makeQuery(id+"F0.imprint","IMPRINT",FACE,{"disambiguationData":[TD([[makeQuery(id+"F0.imprint","IMPRINT",EDGE,{"derivedFrom":sQuery(id+"F0.wireOp",EDGE,"E32.0")}),-1.0]])]});
            var Q4;
            Q4=makeQuery(id+"F0.imprint","IMPRINT",FACE,{"disambiguationData":[TD([[makeQuery(id+"F0.imprint","IMPRINT",EDGE,{"derivedFrom":sQuery(id+"F0.wireOp",EDGE,"E36.0")}),-1.0]])]});
            var Q5;
            Q5=makeQuery(id+"F0.imprint","IMPRINT",FACE,{"disambiguationData":[TD([[makeQuery(id+"F0.imprint","IMPRINT",EDGE,{"derivedFrom":sQuery(id+"F0.wireOp",EDGE,"E38.0")}),-1.0]])]});
            var Q6;
            Q6=makeQuery(id+"F0.imprint","IMPRINT",FACE,{"disambiguationData":[TD([[makeQuery(id+"F0.imprint","IMPRINT",EDGE,{"derivedFrom":sQuery(id+"F0.wireOp",EDGE,"E10.0")}),-1.0]])]});
            var Q7;
            Q7=makeQuery(id+"F0.imprint","IMPRINT",FACE,{"disambiguationData":[TD([[makeQuery(id+"F0.imprint","IMPRINT",EDGE,{"derivedFrom":sQuery(id+"F0.wireOp",EDGE,"E12.0")}),-1.0]])]});
            var Q8;
            Q8=makeQuery(id+"F0.imprint","IMPRINT",FACE,{"disambiguationData":[TD([[makeQuery(id+"F0.imprint","IMPRINT",EDGE,{"derivedFrom":sQuery(id+"F0.wireOp",EDGE,"E14.0")}),-1.0]])]});
            var Q9;
            Q9=makeQuery(id+"F0.imprint","IMPRINT",FACE,{"disambiguationData":[TD([[makeQuery(id+"F0.imprint","IMPRINT",EDGE,{"derivedFrom":sQuery(id+"F0.wireOp",EDGE,"E17.0")}),-1.0]])]});
            var Q10;
            Q10=makeQuery(id+"F0.imprint","IMPRINT",FACE,{"disambiguationData":[TD([[makeQuery(id+"F0.imprint","IMPRINT",EDGE,{"derivedFrom":sQuery(id+"F0.wireOp",EDGE,"E19.0")}),-1.0]])]});
            var Q11;
            Q11=makeQuery(id+"F0.imprint","IMPRINT",FACE,{"disambiguationData":[TD([[makeQuery(id+"F0.imprint","IMPRINT",EDGE,{"derivedFrom":sQuery(id+"F0.wireOp",EDGE,"E23.0")}),-1.0]])]});
            var Q12;
            Q12=makeQuery(id+"F0.imprint","IMPRINT",FACE,{"disambiguationData":[TD([[makeQuery(id+"F0.imprint","IMPRINT",EDGE,{"derivedFrom":sQuery(id+"F0.wireOp",EDGE,"E21.0")}),-1.0]])]});
            var Q13;
            Q13=makeQuery(id+"F0.imprint","IMPRINT",FACE,{"disambiguationData":[TD([[makeQuery(id+"F0.imprint","IMPRINT",EDGE,{"derivedFrom":sQuery(id+"F0.wireOp",EDGE,"E26.0")}),-1.0]])]});
            var Q14;
            Q14=makeQuery(id+"F0.imprint","IMPRINT",FACE,{"disambiguationData":[TD([[makeQuery(id+"F0.imprint","IMPRINT",EDGE,{"derivedFrom":sQuery(id+"F0.wireOp",EDGE,"E50.0")}),-1.0]])]});
            var Q15;
            Q15=makeQuery(id+"F0.imprint","IMPRINT",FACE,{"disambiguationData":[TD([[makeQuery(id+"F0.imprint","IMPRINT",EDGE,{"derivedFrom":sQuery(id+"F0.wireOp",EDGE,"E30.0")}),-1.0]])]});
            var Q16;
            Q16=makeQuery(id+"F0.imprint","IMPRINT",FACE,{"disambiguationData":[TD([[makeQuery(id+"F0.imprint","IMPRINT",EDGE,{"derivedFrom":sQuery(id+"F0.wireOp",EDGE,"E40.0")}),-1.0]])]});
            var Q17;
            Q17=makeQuery(id+"F0.imprint","IMPRINT",FACE,{"disambiguationData":[TD([[makeQuery(id+"F0.imprint","IMPRINT",EDGE,{"derivedFrom":sQuery(id+"F0.wireOp",EDGE,"E42.0")}),-1.0]])]});
            var Q18;
            Q18=makeQuery(id+"F0.imprint","IMPRINT",FACE,{"disambiguationData":[TD([[makeQuery(id+"F0.imprint","IMPRINT",EDGE,{"derivedFrom":sQuery(id+"F0.wireOp",EDGE,"E1.0")}),-1.0]])]});
            var Q19;
            Q19=makeQuery(id+"F0.imprint","IMPRINT",FACE,{"disambiguationData":[TD([[makeQuery(id+"F0.imprint","IMPRINT",EDGE,{"derivedFrom":sQuery(id+"F0.wireOp",EDGE,"E3.0")}),-1.0]])]});
            var Q20;
            Q20=makeQuery(id+"F0.imprint","IMPRINT",FACE,{"disambiguationData":[TD([[makeQuery(id+"F0.imprint","IMPRINT",EDGE,{"derivedFrom":sQuery(id+"F0.wireOp",EDGE,"E44.0")}),-1.0]])]});
            var Q21;
            Q21=makeQuery(id+"F0.imprint","IMPRINT",FACE,{"disambiguationData":[TD([[makeQuery(id+"F0.imprint","IMPRINT",EDGE,{"derivedFrom":sQuery(id+"F0.wireOp",EDGE,"E5.0")}),-1.0]])]});
            var Q22;
            Q22=makeQuery(id+"F0.imprint","IMPRINT",FACE,{"disambiguationData":[TD([[makeQuery(id+"F0.imprint","IMPRINT",EDGE,{"derivedFrom":sQuery(id+"F0.wireOp",EDGE,"E46.0")}),-1.0]])]});
            var Q23;
            Q23=makeQuery(id+"F0.imprint","IMPRINT",FACE,{"disambiguationData":[TD([[makeQuery(id+"F0.imprint","IMPRINT",EDGE,{"derivedFrom":sQuery(id+"F0.wireOp",EDGE,"E8.0")}),-1.0]])]});
            var Q24;
            Q24=makeQuery(id+"F0.imprint","IMPRINT",FACE,{"disambiguationData":[TD([[makeQuery(id+"F0.imprint","IMPRINT",EDGE,{"derivedFrom":sQuery(id+"F0.wireOp",EDGE,"E26.0")}),1.0]])]});
            var Q25;
            Q25=makeQuery(id+"F0.imprint","IMPRINT",FACE,{"disambiguationData":[TD([[makeQuery(id+"F0.imprint","IMPRINT",EDGE,{"derivedFrom":sQuery(id+"F0.wireOp",EDGE,"E5.0")}),1.0]])]});
            var Q26;
            Q26=makeQuery(id+"F0.imprint","IMPRINT",FACE,{"disambiguationData":[TD([[makeQuery(id+"F0.imprint","IMPRINT",EDGE,{"derivedFrom":sQuery(id+"F0.wireOp",EDGE,"E42.0")}),1.0]])]});
            var Q27;
            Q27=makeQuery(id+"F0.imprint","IMPRINT",FACE,{"disambiguationData":[TD([[makeQuery(id+"F0.imprint","IMPRINT",EDGE,{"derivedFrom":sQuery(id+"F0.wireOp",EDGE,"E40.0")}),1.0]])]});
            var Q28;
            Q28=makeQuery(id+"F0.imprint","IMPRINT",FACE,{"disambiguationData":[TD([[makeQuery(id+"F0.imprint","IMPRINT",EDGE,{"derivedFrom":sQuery(id+"F0.wireOp",EDGE,"E8.0")}),1.0]])]});
            var Q29;
            Q29=makeQuery(id+"F0.imprint","IMPRINT",FACE,{"disambiguationData":[TD([[makeQuery(id+"F0.imprint","IMPRINT",EDGE,{"derivedFrom":sQuery(id+"F0.wireOp",EDGE,"E32.0")}),1.0]])]});
            var Q30;
            Q30=makeQuery(id+"F0.imprint","IMPRINT",FACE,{"disambiguationData":[TD([[makeQuery(id+"F0.imprint","IMPRINT",EDGE,{"derivedFrom":sQuery(id+"F0.wireOp",EDGE,"E48.0")}),1.0]])]});
            var Q31;
            Q31=makeQuery(id+"F0.imprint","IMPRINT",FACE,{"disambiguationData":[TD([[makeQuery(id+"F0.imprint","IMPRINT",EDGE,{"derivedFrom":sQuery(id+"F0.wireOp",EDGE,"E19.0")}),1.0]])]});
            var Q32;
            Q32=makeQuery(id+"F0.imprint","IMPRINT",FACE,{"disambiguationData":[TD([[makeQuery(id+"F0.imprint","IMPRINT",EDGE,{"derivedFrom":sQuery(id+"F0.wireOp",EDGE,"E38.0")}),1.0]])]});
            var Q33;
            Q33=makeQuery(id+"F0.imprint","IMPRINT",FACE,{"disambiguationData":[TD([[makeQuery(id+"F0.imprint","IMPRINT",EDGE,{"derivedFrom":sQuery(id+"F0.wireOp",EDGE,"E23.0")}),1.0]])]});
            var Q34;
            Q34=makeQuery(id+"F0.imprint","IMPRINT",FACE,{"disambiguationData":[TD([[makeQuery(id+"F0.imprint","IMPRINT",EDGE,{"derivedFrom":sQuery(id+"F0.wireOp",EDGE,"E46.0")}),1.0]])]});
            var Q35;
            Q35=makeQuery(id+"F0.imprint","IMPRINT",FACE,{"disambiguationData":[TD([[makeQuery(id+"F0.imprint","IMPRINT",EDGE,{"derivedFrom":sQuery(id+"F0.wireOp",EDGE,"E30.0")}),1.0]])]});
            var Q36;
            Q36=makeQuery(id+"F0.imprint","IMPRINT",FACE,{"disambiguationData":[TD([[makeQuery(id+"F0.imprint","IMPRINT",EDGE,{"derivedFrom":sQuery(id+"F0.wireOp",EDGE,"E36.0")}),1.0]])]});
            var Q37;
            Q37=makeQuery(id+"F0.imprint","IMPRINT",FACE,{"disambiguationData":[TD([[makeQuery(id+"F0.imprint","IMPRINT",EDGE,{"derivedFrom":sQuery(id+"F0.wireOp",EDGE,"E14.0")}),1.0]])]});
            var Q38;
            Q38=makeQuery(id+"F0.imprint","IMPRINT",FACE,{"disambiguationData":[TD([[makeQuery(id+"F0.imprint","IMPRINT",EDGE,{"derivedFrom":sQuery(id+"F0.wireOp",EDGE,"E3.0")}),1.0]])]});
            var Q39;
            Q39=makeQuery(id+"F0.imprint","IMPRINT",FACE,{"disambiguationData":[TD([[makeQuery(id+"F0.imprint","IMPRINT",EDGE,{"derivedFrom":sQuery(id+"F0.wireOp",EDGE,"E28.0")}),1.0]])]});
            var Q40;
            Q40=makeQuery(id+"F0.imprint","IMPRINT",FACE,{"disambiguationData":[TD([[makeQuery(id+"F0.imprint","IMPRINT",EDGE,{"derivedFrom":sQuery(id+"F0.wireOp",EDGE,"E17.0")}),1.0]])]});
            var Q41;
            Q41=makeQuery(id+"F0.imprint","IMPRINT",FACE,{"disambiguationData":[TD([[makeQuery(id+"F0.imprint","IMPRINT",EDGE,{"derivedFrom":sQuery(id+"F0.wireOp",EDGE,"E10.0")}),1.0]])]});
            var Q42;
            Q42=makeQuery(id+"F0.imprint","IMPRINT",FACE,{"disambiguationData":[TD([[makeQuery(id+"F0.imprint","IMPRINT",EDGE,{"derivedFrom":sQuery(id+"F0.wireOp",EDGE,"E50.0")}),1.0]])]});
            var Q43;
            Q43=makeQuery(id+"F0.imprint","IMPRINT",FACE,{"disambiguationData":[TD([[makeQuery(id+"F0.imprint","IMPRINT",EDGE,{"derivedFrom":sQuery(id+"F0.wireOp",EDGE,"E21.0")}),1.0]])]});
            var Q44;
            Q44=makeQuery(id+"F0.imprint","IMPRINT",FACE,{"disambiguationData":[TD([[makeQuery(id+"F0.imprint","IMPRINT",EDGE,{"derivedFrom":sQuery(id+"F0.wireOp",EDGE,"E34.0")}),1.0]])]});
            var Q45;
            Q45=makeQuery(id+"F0.imprint","IMPRINT",FACE,{"disambiguationData":[TD([[makeQuery(id+"F0.imprint","IMPRINT",EDGE,{"derivedFrom":sQuery(id+"F0.wireOp",EDGE,"E44.0")}),1.0]])]});
            var Q46;
            Q46=makeQuery(id+"F0.imprint","IMPRINT",FACE,{"disambiguationData":[TD([[makeQuery(id+"F0.imprint","IMPRINT",EDGE,{"derivedFrom":sQuery(id+"F0.wireOp",EDGE,"E1.0")}),1.0]])]});
            var Q47;
            Q47=makeQuery(id+"F0.imprint","IMPRINT",FACE,{"disambiguationData":[TD([[makeQuery(id+"F0.imprint","IMPRINT",EDGE,{"derivedFrom":sQuery(id+"F0.wireOp",EDGE,"E12.0")}),1.0]])]});
            extrude(context, id + "F1", {"entities" : qUnion([Q0, Q1, Q2, Q3, Q4, Q5, Q6, Q7, Q8, Q9, Q10, Q11, Q12, Q13, Q14, Q15, Q16, Q17, Q18, Q19, Q20, Q21, Q22, Q23, Q24, Q25, Q26, Q27, Q28, Q29, Q30, Q31, Q32, Q33, Q34, Q35, Q36, Q37, Q38, Q39, Q40, Q41, Q42, Q43, Q44, Q45, Q46, Q47]), "depth" : 12.7 * mm});
        }
        {
            var Q0;
            Q0=makeQuery(id+"F0.imprint","IMPRINT",FACE,{"disambiguationData":[TD([[makeQuery(id+"F0.imprint","IMPRINT",EDGE,{"derivedFrom":sQuery(id+"F0.wireOp",EDGE,"E36.0")}),1.0]])]});
            var Q1;
            Q1=makeQuery(id+"F0.imprint","IMPRINT",FACE,{"disambiguationData":[TD([[makeQuery(id+"F0.imprint","IMPRINT",EDGE,{"derivedFrom":sQuery(id+"F0.wireOp",EDGE,"E30.0")}),1.0]])]});
            var Q2;
            Q2=makeQuery(id+"F0.imprint","IMPRINT",FACE,{"disambiguationData":[TD([[makeQuery(id+"F0.imprint","IMPRINT",EDGE,{"derivedFrom":sQuery(id+"F0.wireOp",EDGE,"E34.0")}),1.0]])]});
            var Q3;
            Q3=makeQuery(id+"F0.imprint","IMPRINT",FACE,{"disambiguationData":[TD([[makeQuery(id+"F0.imprint","IMPRINT",EDGE,{"derivedFrom":sQuery(id+"F0.wireOp",EDGE,"E28.0")}),1.0]])]});
            var Q4;
            Q4=makeQuery(id+"F0.imprint","IMPRINT",FACE,{"disambiguationData":[TD([[makeQuery(id+"F0.imprint","IMPRINT",EDGE,{"derivedFrom":sQuery(id+"F0.wireOp",EDGE,"E17.0")}),1.0]])]});
            var Q5;
            Q5=makeQuery(id+"F0.imprint","IMPRINT",FACE,{"disambiguationData":[TD([[makeQuery(id+"F0.imprint","IMPRINT",EDGE,{"derivedFrom":sQuery(id+"F0.wireOp",EDGE,"E26.0")}),1.0]])]});
            var Q6;
            Q6=makeQuery(id+"F0.imprint","IMPRINT",FACE,{"disambiguationData":[TD([[makeQuery(id+"F0.imprint","IMPRINT",EDGE,{"derivedFrom":sQuery(id+"F0.wireOp",EDGE,"E8.0")}),1.0]])]});
            var Q7;
            Q7=makeQuery(id+"F0.imprint","IMPRINT",FACE,{"disambiguationData":[TD([[makeQuery(id+"F0.imprint","IMPRINT",EDGE,{"derivedFrom":sQuery(id+"F0.wireOp",EDGE,"E1.0")}),1.0]])]});
            var Q8;
            Q8=makeQuery(id+"F0.imprint","IMPRINT",FACE,{"disambiguationData":[TD([[makeQuery(id+"F0.imprint","IMPRINT",EDGE,{"derivedFrom":sQuery(id+"F0.wireOp",EDGE,"E12.0")}),1.0]])]});
            var Q9;
            Q9=makeQuery(id+"F0.imprint","IMPRINT",FACE,{"disambiguationData":[TD([[makeQuery(id+"F0.imprint","IMPRINT",EDGE,{"derivedFrom":sQuery(id+"F0.wireOp",EDGE,"E38.0")}),1.0]])]});
            var Q10;
            Q10=makeQuery(id+"F0.imprint","IMPRINT",FACE,{"disambiguationData":[TD([[makeQuery(id+"F0.imprint","IMPRINT",EDGE,{"derivedFrom":sQuery(id+"F0.wireOp",EDGE,"E44.0")}),1.0]])]});
            var Q11;
            Q11=makeQuery(id+"F0.imprint","IMPRINT",FACE,{"disambiguationData":[TD([[makeQuery(id+"F0.imprint","IMPRINT",EDGE,{"derivedFrom":sQuery(id+"F0.wireOp",EDGE,"E42.0")}),1.0]])]});
            var Q12;
            Q12=makeQuery(id+"F0.imprint","IMPRINT",FACE,{"disambiguationData":[TD([[makeQuery(id+"F0.imprint","IMPRINT",EDGE,{"derivedFrom":sQuery(id+"F0.wireOp",EDGE,"E50.0")}),1.0]])]});
            var Q13;
            Q13=makeQuery(id+"F0.imprint","IMPRINT",FACE,{"disambiguationData":[TD([[makeQuery(id+"F0.imprint","IMPRINT",EDGE,{"derivedFrom":sQuery(id+"F0.wireOp",EDGE,"E48.0")}),1.0]])]});
            var Q14;
            Q14=makeQuery(id+"F0.imprint","IMPRINT",FACE,{"disambiguationData":[TD([[makeQuery(id+"F0.imprint","IMPRINT",EDGE,{"derivedFrom":sQuery(id+"F0.wireOp",EDGE,"E46.0")}),1.0]])]});
            var Q15;
            Q15=makeQuery(id+"F0.imprint","IMPRINT",FACE,{"disambiguationData":[TD([[makeQuery(id+"F0.imprint","IMPRINT",EDGE,{"derivedFrom":sQuery(id+"F0.wireOp",EDGE,"E40.0")}),1.0]])]});
            var Q16;
            Q16=makeQuery(id+"F0.imprint","IMPRINT",FACE,{"disambiguationData":[TD([[makeQuery(id+"F0.imprint","IMPRINT",EDGE,{"derivedFrom":sQuery(id+"F0.wireOp",EDGE,"E19.0")}),1.0]])]});
            var Q17;
            Q17=makeQuery(id+"F0.imprint","IMPRINT",FACE,{"disambiguationData":[TD([[makeQuery(id+"F0.imprint","IMPRINT",EDGE,{"derivedFrom":sQuery(id+"F0.wireOp",EDGE,"E3.0")}),1.0]])]});
            var Q18;
            Q18=makeQuery(id+"F0.imprint","IMPRINT",FACE,{"disambiguationData":[TD([[makeQuery(id+"F0.imprint","IMPRINT",EDGE,{"derivedFrom":sQuery(id+"F0.wireOp",EDGE,"E23.0")}),1.0]])]});
            var Q19;
            Q19=makeQuery(id+"F0.imprint","IMPRINT",FACE,{"disambiguationData":[TD([[makeQuery(id+"F0.imprint","IMPRINT",EDGE,{"derivedFrom":sQuery(id+"F0.wireOp",EDGE,"E21.0")}),1.0]])]});
            var Q20;
            Q20=makeQuery(id+"F0.imprint","IMPRINT",FACE,{"disambiguationData":[TD([[makeQuery(id+"F0.imprint","IMPRINT",EDGE,{"derivedFrom":sQuery(id+"F0.wireOp",EDGE,"E10.0")}),1.0]])]});
            var Q21;
            Q21=makeQuery(id+"F0.imprint","IMPRINT",FACE,{"disambiguationData":[TD([[makeQuery(id+"F0.imprint","IMPRINT",EDGE,{"derivedFrom":sQuery(id+"F0.wireOp",EDGE,"E32.0")}),1.0]])]});
            var Q22;
            Q22=makeQuery(id+"F0.imprint","IMPRINT",FACE,{"disambiguationData":[TD([[makeQuery(id+"F0.imprint","IMPRINT",EDGE,{"derivedFrom":sQuery(id+"F0.wireOp",EDGE,"E14.0")}),1.0]])]});
            var Q23;
            Q23=makeQuery(id+"F0.imprint","IMPRINT",FACE,{"disambiguationData":[TD([[makeQuery(id+"F0.imprint","IMPRINT",EDGE,{"derivedFrom":sQuery(id+"F0.wireOp",EDGE,"E5.0")}),1.0]])]});
            var Q24;
            {var subQ6=sQuery(id+"F0.wireOp",EDGE,"E2.3");Q24=makeQuery(id+"F0.imprint","IMPRINT",FACE,{"disambiguationData":[TD([[makeQuery(id+"F0.imprint","IMPRINT",EDGE,{"derivedFrom":subQ6}),1.0]])]});}
            var Q25;
            Q25=makeQuery(id+"F0.imprint","IMPRINT",FACE,{"disambiguationData":[TD([[makeQuery(id+"F0.imprint","IMPRINT",EDGE,{"derivedFrom":sQuery(id+"F0.wireOp",EDGE,"E2.1")}),1.0]])]});
            extrude(context, id + "F2", {"entities" : qUnion([Q0, Q1, Q2, Q3, Q4, Q5, Q6, Q7, Q8, Q9, Q10, Q11, Q12, Q13, Q14, Q15, Q16, Q17, Q18, Q19, Q20, Q21, Q22, Q23, Q24, Q25]), "operationType" : NewBodyOperationType.ADD, "depth" : 95.25 * mm});
        }
    });
